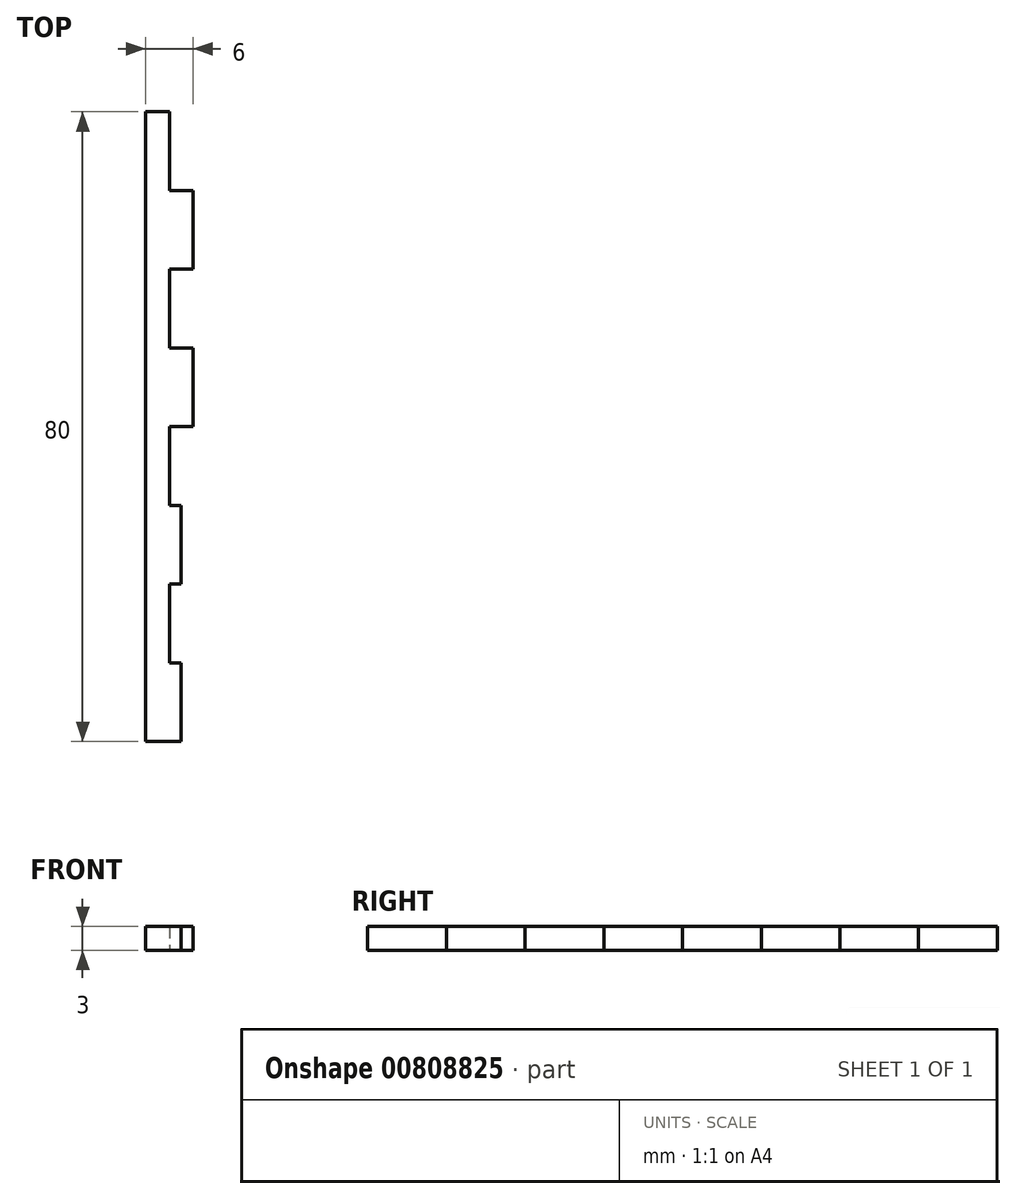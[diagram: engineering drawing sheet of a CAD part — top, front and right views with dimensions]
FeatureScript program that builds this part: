
annotation { "Feature Type Name" : "Feature", "Feature Type Description" : "" }
export const myFeature = defineFeature(function(context is Context, id is Id, definition is map)
    precondition{}
    {
        {
            var Q0;
            Q0=qCreatedBy(makeId("Top.planeOp"),FACE);
            var sketch = newSketch(context, id + "F0", { "sketchPlane" : qUnion([Q0])});
            skLineSegment(sketch, "E0.bottom", {"start": v(-14.93, 40) * mm, "end": v(14.93, 40) * mm});
            skLineSegment(sketch, "E0.top", {"start": v(-14.93, -40) * mm, "end": v(14.93, -40) * mm});
            skLineSegment(sketch, "E0.left", {"start": v(-14.93, 40) * mm, "end": v(-14.93, -40) * mm});
            skLineSegment(sketch, "E0.right", {"start": v(14.93, 40) * mm, "end": v(14.93, -40) * mm});
            skPoint(sketch, "E0.middle", {"position": v(0, 0) * mm});
            skLineSegment(sketch, "E1.bottom", {"start": v(13.34, -40) * mm, "end": v(10.34, -40) * mm});
            skLineSegment(sketch, "E1.top", {"start": v(13.34, -43) * mm, "end": v(10.34, -43) * mm});
            skLineSegment(sketch, "E1.left", {"start": v(13.34, -40) * mm, "end": v(13.34, -43) * mm});
            skLineSegment(sketch, "E1.right", {"start": v(10.34, -40) * mm, "end": v(10.34, -43) * mm});
            skLineSegment(sketch, "E2.bottom", {"start": v(7.34, -40) * mm, "end": v(4.34, -40) * mm});
            skLineSegment(sketch, "E2.top", {"start": v(7.34, -43) * mm, "end": v(4.34, -43) * mm});
            skLineSegment(sketch, "E2.left", {"start": v(7.34, -40) * mm, "end": v(7.34, -43) * mm});
            skLineSegment(sketch, "E2.right", {"start": v(4.34, -40) * mm, "end": v(4.34, -43) * mm});
            skLineSegment(sketch, "E3.bottom", {"start": v(1.34, -40) * mm, "end": v(-1.66, -40) * mm});
            skLineSegment(sketch, "E3.top", {"start": v(1.34, -43) * mm, "end": v(-1.66, -43) * mm});
            skLineSegment(sketch, "E3.left", {"start": v(1.34, -40) * mm, "end": v(1.34, -43) * mm});
            skLineSegment(sketch, "E3.right", {"start": v(-1.66, -40) * mm, "end": v(-1.66, -43) * mm});
            skLineSegment(sketch, "E4.bottom", {"start": v(14.93, -40) * mm, "end": v(11.93, -40) * mm});
            skLineSegment(sketch, "E4.top", {"start": v(14.93, -30) * mm, "end": v(11.93, -30) * mm});
            skLineSegment(sketch, "E4.left", {"start": v(14.93, -40) * mm, "end": v(14.93, -30) * mm});
            skLineSegment(sketch, "E4.right", {"start": v(11.93, -40) * mm, "end": v(11.93, -30) * mm});
            skLineSegment(sketch, "E5.0.1.0", {"start": v(11.93, -30) * mm, "end": v(11.93, -20) * mm});
            skLineSegment(sketch, "E5.0.1.1", {"start": v(14.93, -20) * mm, "end": v(11.93, -20) * mm});
            skLineSegment(sketch, "E5.0.1.3", {"start": v(14.93, -30) * mm, "end": v(14.93, -20) * mm});
            skLineSegment(sketch, "E5.0.2.0", {"start": v(11.93, -20) * mm, "end": v(11.93, -10) * mm});
            skLineSegment(sketch, "E5.0.2.1", {"start": v(14.93, -10) * mm, "end": v(11.93, -10) * mm});
            skLineSegment(sketch, "E5.0.2.2", {"start": v(14.93, -20) * mm, "end": v(11.93, -20) * mm});
            skLineSegment(sketch, "E5.0.2.3", {"start": v(14.93, -20) * mm, "end": v(14.93, -10) * mm});
            skLineSegment(sketch, "E5.0.3.0", {"start": v(11.93, -10) * mm, "end": v(11.93, 0) * mm});
            skLineSegment(sketch, "E5.0.3.1", {"start": v(14.93, 0) * mm, "end": v(11.93, 0) * mm});
            skLineSegment(sketch, "E5.0.3.2", {"start": v(14.93, -10) * mm, "end": v(11.93, -10) * mm});
            skLineSegment(sketch, "E5.0.3.3", {"start": v(14.93, -10) * mm, "end": v(14.93, 0) * mm});
            skLineSegment(sketch, "E5.0.4.0", {"start": v(11.93, 0) * mm, "end": v(11.93, 10) * mm});
            skLineSegment(sketch, "E5.0.4.1", {"start": v(14.93, 10) * mm, "end": v(11.93, 10) * mm});
            skLineSegment(sketch, "E5.0.4.2", {"start": v(14.93, 0) * mm, "end": v(11.93, 0) * mm});
            skLineSegment(sketch, "E5.0.4.3", {"start": v(14.93, 0) * mm, "end": v(14.93, 10) * mm});
            skLineSegment(sketch, "E5.0.5.0", {"start": v(11.93, 10) * mm, "end": v(11.93, 20) * mm});
            skLineSegment(sketch, "E5.0.5.1", {"start": v(14.93, 20) * mm, "end": v(11.93, 20) * mm});
            skLineSegment(sketch, "E5.0.5.2", {"start": v(14.93, 10) * mm, "end": v(11.93, 10) * mm});
            skLineSegment(sketch, "E5.0.5.3", {"start": v(14.93, 10) * mm, "end": v(14.93, 20) * mm});
            skLineSegment(sketch, "E5.0.6.0", {"start": v(11.93, 20) * mm, "end": v(11.93, 30) * mm});
            skLineSegment(sketch, "E5.0.6.1", {"start": v(14.93, 30) * mm, "end": v(11.93, 30) * mm});
            skLineSegment(sketch, "E5.0.6.2", {"start": v(14.93, 20) * mm, "end": v(11.93, 20) * mm});
            skLineSegment(sketch, "E5.0.6.3", {"start": v(14.93, 20) * mm, "end": v(14.93, 30) * mm});
            skLineSegment(sketch, "E5.0.7.0", {"start": v(11.93, 30) * mm, "end": v(11.93, 40) * mm});
            skLineSegment(sketch, "E5.0.7.1", {"start": v(14.93, 40) * mm, "end": v(11.93, 40) * mm});
            skLineSegment(sketch, "E5.0.7.2", {"start": v(14.93, 30) * mm, "end": v(11.93, 30) * mm});
            skLineSegment(sketch, "E5.0.7.3", {"start": v(14.93, 30) * mm, "end": v(14.93, 40) * mm});
            skLineSegment(sketch, "E5.direction1", {"start": v(11.93, -40) * mm, "end": v(36.93, -40) * mm, "construction": true});
            skLineSegment(sketch, "E5.direction2", {"start": v(11.93, -40) * mm, "end": v(11.93, -30) * mm, "construction": true});
            skLineSegment(sketch, "E6.MirrorCS", {"start": v(14.93, 10) * mm, "end": v(17.93, 10) * mm});
            skLineSegment(sketch, "E7.MirrorCS", {"start": v(14.93, -30) * mm, "end": v(17.93, -30) * mm});
            skLineSegment(sketch, "E8.MirrorCS", {"start": v(14.93, -10) * mm, "end": v(17.93, -10) * mm});
            skLineSegment(sketch, "E9.MirrorCS", {"start": v(14.93, 30) * mm, "end": v(17.93, 30) * mm});
            skLineSegment(sketch, "E10.MirrorCS", {"start": v(14.93, 0) * mm, "end": v(17.93, 0) * mm});
            skLineSegment(sketch, "E11.MirrorCS", {"start": v(44.8, -40) * mm, "end": v(14.93, -40) * mm});
            skLineSegment(sketch, "E12.MirrorCS", {"start": v(14.93, 20) * mm, "end": v(17.93, 20) * mm});
            skLineSegment(sketch, "E13.MirrorCS", {"start": v(14.93, -20) * mm, "end": v(17.93, -20) * mm});
            skLineSegment(sketch, "E14.MirrorCS", {"start": v(14.93, -40) * mm, "end": v(17.93, -40) * mm});
            skLineSegment(sketch, "E15.MirrorCS", {"start": v(16.53, -40) * mm, "end": v(19.53, -40) * mm});
            skLineSegment(sketch, "E16.MirrorCS", {"start": v(16.53, -40) * mm, "end": v(16.53, -43) * mm});
            skLineSegment(sketch, "E17.MirrorCS", {"start": v(16.53, -43) * mm, "end": v(19.53, -43) * mm});
            skLineSegment(sketch, "E18.MirrorCS", {"start": v(14.93, 40) * mm, "end": v(17.93, 40) * mm});
            skLineSegment(sketch, "E19.MirrorCS", {"start": v(44.8, 40) * mm, "end": v(14.93, 40) * mm});
            skLineSegment(sketch, "E20.MirrorCS", {"start": v(19.53, -40) * mm, "end": v(19.53, -43) * mm});
            skLineSegment(sketch, "E21.MirrorCS", {"start": v(17.93, -40) * mm, "end": v(17.93, -30) * mm});
            skLineSegment(sketch, "E22.MirrorCS", {"start": v(17.93, -40) * mm, "end": v(-7.07, -40) * mm, "construction": true});
            skLineSegment(sketch, "E23.MirrorCS", {"start": v(17.93, -40) * mm, "end": v(17.93, -30) * mm, "construction": true});
            skLineSegment(sketch, "E24.MirrorCS", {"start": v(17.93, -20) * mm, "end": v(17.93, -10) * mm});
            skLineSegment(sketch, "E25.MirrorCS", {"start": v(17.93, 20) * mm, "end": v(17.93, 30) * mm});
            skLineSegment(sketch, "E26.MirrorCS", {"start": v(17.93, -10) * mm, "end": v(17.93, 0) * mm});
            skLineSegment(sketch, "E27.MirrorCS", {"start": v(17.93, 30) * mm, "end": v(17.93, 40) * mm});
            skLineSegment(sketch, "E28.MirrorCS", {"start": v(17.93, 0) * mm, "end": v(17.93, 10) * mm});
            skLineSegment(sketch, "E29.MirrorCS", {"start": v(17.93, 10) * mm, "end": v(17.93, 20) * mm});
            skLineSegment(sketch, "E30.MirrorCS", {"start": v(17.93, -30) * mm, "end": v(17.93, -20) * mm});
            skSolve(sketch);
        }
        {
            var Q0;
            Q0=makeQuery(id+"F0.imprint","IMPRINT",FACE,{"disambiguationData":[TD([[makeQuery(id+"F0.imprint","IMPRINT",EDGE,{"derivedFrom":sQuery(id+"F0.wireOp",EDGE,"E3.bottom")}),1.0]])]});
            var Q1;
            Q1=makeQuery(id+"F0.imprint","IMPRINT",FACE,{"disambiguationData":[TD([[makeQuery(id+"F0.imprint","IMPRINT",EDGE,{"derivedFrom":sQuery(id+"F0.wireOp",EDGE,"E2.bottom")}),1.0]])]});
            var Q2;
            Q2=makeQuery(id+"F0.imprint","IMPRINT",FACE,{"disambiguationData":[TD([[makeQuery(id+"F0.imprint","IMPRINT",EDGE,{"derivedFrom":sQuery(id+"F0.wireOp",EDGE,"E0.bottom")}),-1.0]])]});
            var Q3;
            {var subQ1=sQuery(id+"F0.wireOp",EDGE,"E4.right");Q3=makeQuery(id+"F0.imprint","IMPRINT",FACE,{"disambiguationData":[TD([[makeQuery(id+"F0.imprint","IMPRINT",EDGE,{"derivedFrom":subQ1}),-1.0]])]});}
            var Q4;
            Q4=makeQuery(id+"F0.imprint","IMPRINT",FACE,{"disambiguationData":[TD([[makeQuery(id+"F0.imprint","IMPRINT",EDGE,{"derivedFrom":sQuery(id+"F0.wireOp",EDGE,"E5.0.1.0")}),-1.0]])]});
            var Q5;
            {var subQ4=sQuery(id+"F0.wireOp",EDGE,"E7.MirrorCS");Q5=makeQuery(id+"F0.imprint","IMPRINT",FACE,{"disambiguationData":[TD([[makeQuery(id+"F0.imprint","IMPRINT",EDGE,{"derivedFrom":subQ4}),-1.0]])]});}
            var Q6;
            {var subQ2=sQuery(id+"F0.wireOp",EDGE,"E1.bottom");Q6=makeQuery(id+"F0.imprint","IMPRINT",FACE,{"disambiguationData":[TD([[makeQuery(id+"F0.imprint","IMPRINT",EDGE,{"derivedFrom":subQ2}),1.0]])]});}
            var Q7;
            Q7=makeQuery(id+"F0.imprint","IMPRINT",FACE,{"disambiguationData":[TD([[makeQuery(id+"F0.imprint","IMPRINT",EDGE,{"derivedFrom":sQuery(id+"F0.wireOp",EDGE,"E5.0.2.0")}),-1.0]])]});
            var Q8;
            {var subQ0=sQuery(id+"F0.wireOp",EDGE,"E8.MirrorCS");Q8=makeQuery(id+"F0.imprint","IMPRINT",FACE,{"disambiguationData":[TD([[makeQuery(id+"F0.imprint","IMPRINT",EDGE,{"derivedFrom":subQ0}),-1.0]])]});}
            var Q9;
            Q9=makeQuery(id+"F0.imprint","IMPRINT",FACE,{"disambiguationData":[TD([[makeQuery(id+"F0.imprint","IMPRINT",EDGE,{"derivedFrom":sQuery(id+"F0.wireOp",EDGE,"E5.0.3.0")}),-1.0]])]});
            var Q10;
            {var subQ0=sQuery(id+"F0.wireOp",EDGE,"E10.MirrorCS");Q10=makeQuery(id+"F0.imprint","IMPRINT",FACE,{"disambiguationData":[TD([[makeQuery(id+"F0.imprint","IMPRINT",EDGE,{"derivedFrom":subQ0}),1.0]])]});}
            var Q11;
            Q11=makeQuery(id+"F0.imprint","IMPRINT",FACE,{"disambiguationData":[TD([[makeQuery(id+"F0.imprint","IMPRINT",EDGE,{"derivedFrom":sQuery(id+"F0.wireOp",EDGE,"E5.0.4.0")}),-1.0]])]});
            var Q12;
            Q12=makeQuery(id+"F0.imprint","IMPRINT",FACE,{"disambiguationData":[TD([[makeQuery(id+"F0.imprint","IMPRINT",EDGE,{"derivedFrom":sQuery(id+"F0.wireOp",EDGE,"E5.0.5.0")}),-1.0]])]});
            var Q13;
            Q13=makeQuery(id+"F0.imprint","IMPRINT",FACE,{"disambiguationData":[TD([[makeQuery(id+"F0.imprint","IMPRINT",EDGE,{"derivedFrom":sQuery(id+"F0.wireOp",EDGE,"E5.0.6.0")}),-1.0]])]});
            var Q14;
            {var subQ0=sQuery(id+"F0.wireOp",EDGE,"E9.MirrorCS");Q14=makeQuery(id+"F0.imprint","IMPRINT",FACE,{"disambiguationData":[TD([[makeQuery(id+"F0.imprint","IMPRINT",EDGE,{"derivedFrom":subQ0}),-1.0]])]});}
            var Q15;
            Q15=makeQuery(id+"F0.imprint","IMPRINT",FACE,{"disambiguationData":[TD([[makeQuery(id+"F0.imprint","IMPRINT",EDGE,{"derivedFrom":sQuery(id+"F0.wireOp",EDGE,"E5.0.7.0")}),-1.0]])]});
            extrude(context, id + "F1", {"entities" : qUnion([Q0, Q1, Q2, Q3, Q4, Q5, Q6, Q7, Q8, Q9, Q10, Q11, Q12, Q13, Q14, Q15]), "depth" : 3 * mm, "offsetDistance" : 25 * mm});
        }
        {
            var Q0;
            Q0=makeQuery(id+"F1.opExtrude","CAP_FACE",FACE,{"disambiguationData":[OSD([sQuery(id+"F0.wireOp",EDGE,"E0.bottom"),sQuery(id+"F0.wireOp",EDGE,"E0.top"),sQuery(id+"F0.wireOp",EDGE,"E0.left"),sQuery(id+"F0.wireOp",EDGE,"E1.top"),sQuery(id+"F0.wireOp",EDGE,"E1.left"),sQuery(id+"F0.wireOp",EDGE,"E1.right"),sQuery(id+"F0.wireOp",EDGE,"E2.top"),sQuery(id+"F0.wireOp",EDGE,"E2.left"),sQuery(id+"F0.wireOp",EDGE,"E2.right"),sQuery(id+"F0.wireOp",EDGE,"E3.top"),sQuery(id+"F0.wireOp",EDGE,"E3.left"),sQuery(id+"F0.wireOp",EDGE,"E3.right"),sQuery(id+"F0.wireOp",EDGE,"E4.bottom"),sQuery(id+"F0.wireOp",EDGE,"E5.0.7.1"),sQuery(id+"F0.wireOp",EDGE,"E10.MirrorCS"),sQuery(id+"F0.wireOp",EDGE,"E6.MirrorCS"),sQuery(id+"F0.wireOp",EDGE,"E7.MirrorCS"),sQuery(id+"F0.wireOp",EDGE,"E8.MirrorCS"),sQuery(id+"F0.wireOp",EDGE,"E9.MirrorCS"),sQuery(id+"F0.wireOp",EDGE,"E12.MirrorCS"),sQuery(id+"F0.wireOp",EDGE,"E13.MirrorCS"),sQuery(id+"F0.wireOp",EDGE,"E14.MirrorCS"),sQuery(id+"F0.wireOp",EDGE,"E15.MirrorCS"),sQuery(id+"F0.wireOp",EDGE,"E21.MirrorCS"),sQuery(id+"F0.wireOp",EDGE,"E24.MirrorCS"),sQuery(id+"F0.wireOp",EDGE,"E25.MirrorCS"),sQuery(id+"F0.wireOp",EDGE,"E28.MirrorCS"),sQuery(id+"F0.wireOp",EDGE,"E0.right")])],"isStart":false});
            var sketch = newSketch(context, id + "F2", { "sketchPlane" : qUnion([Q0])});
            skLineSegment(sketch, "E31.bottom", {"start": v(-14.93, 40) * mm, "end": v(-6.93, 40) * mm});
            skLineSegment(sketch, "E31.top", {"start": v(-14.93, -40) * mm, "end": v(-6.93, -40) * mm});
            skLineSegment(sketch, "E31.left", {"start": v(-14.93, 40) * mm, "end": v(-14.93, -40) * mm});
            skLineSegment(sketch, "E31.right", {"start": v(-6.93, 40) * mm, "end": v(-6.93, -40) * mm});
            skSolve(sketch);
        }
        {
            var Q0;
            Q0=qSketchRegion(id+"F2",true);
            extrude(context, id + "F3", {"entities" : qUnion([Q0]), "operationType" : NewBodyOperationType.REMOVE, "oppositeDirection" : true, "depth" : 25 * mm, "offsetDistance" : 25 * mm});
        }
        {
            var Q0;
            Q0=makeQuery(id+"F1.opExtrude","CAP_FACE",FACE,{"disambiguationData":[OSD([sQuery(id+"F0.wireOp",EDGE,"E0.bottom"),sQuery(id+"F0.wireOp",EDGE,"E0.top"),sQuery(id+"F0.wireOp",EDGE,"E0.left"),sQuery(id+"F0.wireOp",EDGE,"E1.top"),sQuery(id+"F0.wireOp",EDGE,"E1.left"),sQuery(id+"F0.wireOp",EDGE,"E1.right"),sQuery(id+"F0.wireOp",EDGE,"E2.top"),sQuery(id+"F0.wireOp",EDGE,"E2.left"),sQuery(id+"F0.wireOp",EDGE,"E2.right"),sQuery(id+"F0.wireOp",EDGE,"E3.top"),sQuery(id+"F0.wireOp",EDGE,"E3.left"),sQuery(id+"F0.wireOp",EDGE,"E3.right"),sQuery(id+"F0.wireOp",EDGE,"E4.bottom"),sQuery(id+"F0.wireOp",EDGE,"E5.0.7.1"),sQuery(id+"F0.wireOp",EDGE,"E10.MirrorCS"),sQuery(id+"F0.wireOp",EDGE,"E6.MirrorCS"),sQuery(id+"F0.wireOp",EDGE,"E7.MirrorCS"),sQuery(id+"F0.wireOp",EDGE,"E8.MirrorCS"),sQuery(id+"F0.wireOp",EDGE,"E9.MirrorCS"),sQuery(id+"F0.wireOp",EDGE,"E12.MirrorCS"),sQuery(id+"F0.wireOp",EDGE,"E13.MirrorCS"),sQuery(id+"F0.wireOp",EDGE,"E14.MirrorCS"),sQuery(id+"F0.wireOp",EDGE,"E15.MirrorCS"),sQuery(id+"F0.wireOp",EDGE,"E21.MirrorCS"),sQuery(id+"F0.wireOp",EDGE,"E24.MirrorCS"),sQuery(id+"F0.wireOp",EDGE,"E25.MirrorCS"),sQuery(id+"F0.wireOp",EDGE,"E28.MirrorCS"),sQuery(id+"F0.wireOp",EDGE,"E0.right")])],"isStart":false});
            var sketch = newSketch(context, id + "F4", { "sketchPlane" : qUnion([Q0])});
            skLineSegment(sketch, "E32.bottom", {"start": v(17.93, -40) * mm, "end": v(16.43, -40) * mm});
            skLineSegment(sketch, "E32.top", {"start": v(17.93, -30) * mm, "end": v(16.43, -30) * mm});
            skLineSegment(sketch, "E32.left", {"start": v(17.93, -40) * mm, "end": v(17.93, -30) * mm});
            skLineSegment(sketch, "E32.right", {"start": v(16.43, -40) * mm, "end": v(16.43, -30) * mm});
            skLineSegment(sketch, "E33.bottom", {"start": v(17.93, -20) * mm, "end": v(16.43, -20) * mm});
            skLineSegment(sketch, "E33.top", {"start": v(17.93, -10) * mm, "end": v(16.43, -10) * mm});
            skLineSegment(sketch, "E33.left", {"start": v(17.93, -20) * mm, "end": v(17.93, -10) * mm});
            skLineSegment(sketch, "E33.right", {"start": v(16.43, -20) * mm, "end": v(16.43, -10) * mm});
            skSolve(sketch);
        }
        {
            var Q0;
            Q0=qSketchRegion(id+"F4",true);
            extrude(context, id + "F5", {"entities" : qUnion([Q0]), "operationType" : NewBodyOperationType.REMOVE, "oppositeDirection" : true, "depth" : 25 * mm, "offsetDistance" : 25 * mm});
        }
        {
            var Q0;
            Q0=makeQuery(id+"F1.opExtrude","CAP_FACE",FACE,{"disambiguationData":[OSD([sQuery(id+"F0.wireOp",EDGE,"E0.bottom"),sQuery(id+"F0.wireOp",EDGE,"E0.top"),sQuery(id+"F0.wireOp",EDGE,"E0.left"),sQuery(id+"F0.wireOp",EDGE,"E1.top"),sQuery(id+"F0.wireOp",EDGE,"E1.left"),sQuery(id+"F0.wireOp",EDGE,"E1.right"),sQuery(id+"F0.wireOp",EDGE,"E2.top"),sQuery(id+"F0.wireOp",EDGE,"E2.left"),sQuery(id+"F0.wireOp",EDGE,"E2.right"),sQuery(id+"F0.wireOp",EDGE,"E3.top"),sQuery(id+"F0.wireOp",EDGE,"E3.left"),sQuery(id+"F0.wireOp",EDGE,"E3.right"),sQuery(id+"F0.wireOp",EDGE,"E4.bottom"),sQuery(id+"F0.wireOp",EDGE,"E5.0.7.1"),sQuery(id+"F0.wireOp",EDGE,"E10.MirrorCS"),sQuery(id+"F0.wireOp",EDGE,"E6.MirrorCS"),sQuery(id+"F0.wireOp",EDGE,"E7.MirrorCS"),sQuery(id+"F0.wireOp",EDGE,"E8.MirrorCS"),sQuery(id+"F0.wireOp",EDGE,"E9.MirrorCS"),sQuery(id+"F0.wireOp",EDGE,"E12.MirrorCS"),sQuery(id+"F0.wireOp",EDGE,"E13.MirrorCS"),sQuery(id+"F0.wireOp",EDGE,"E14.MirrorCS"),sQuery(id+"F0.wireOp",EDGE,"E15.MirrorCS"),sQuery(id+"F0.wireOp",EDGE,"E21.MirrorCS"),sQuery(id+"F0.wireOp",EDGE,"E24.MirrorCS"),sQuery(id+"F0.wireOp",EDGE,"E25.MirrorCS"),sQuery(id+"F0.wireOp",EDGE,"E28.MirrorCS"),sQuery(id+"F0.wireOp",EDGE,"E0.right")])],"isStart":false});
            var sketch = newSketch(context, id + "F6", { "sketchPlane" : qUnion([Q0])});
            skLineSegment(sketch, "E34.bottom", {"start": v(-3.03, -15) * mm, "end": v(-6.03, -15) * mm});
            skLineSegment(sketch, "E34.top", {"start": v(-3.03, -5) * mm, "end": v(-6.03, -5) * mm});
            skLineSegment(sketch, "E34.left", {"start": v(-3.03, -15) * mm, "end": v(-3.03, -5) * mm});
            skLineSegment(sketch, "E34.right", {"start": v(-6.03, -15) * mm, "end": v(-6.03, -5) * mm});
            skPoint(sketch, "E34.middle", {"position": v(-4.53, -10) * mm});
            skSolve(sketch);
        }
        {
            var Q0;
            Q0=qSketchRegion(id+"F6",true);
            extrude(context, id + "F7", {"entities" : qUnion([Q0]), "operationType" : NewBodyOperationType.REMOVE, "oppositeDirection" : true, "depth" : 25 * mm, "offsetDistance" : 25 * mm});
        }
    });
